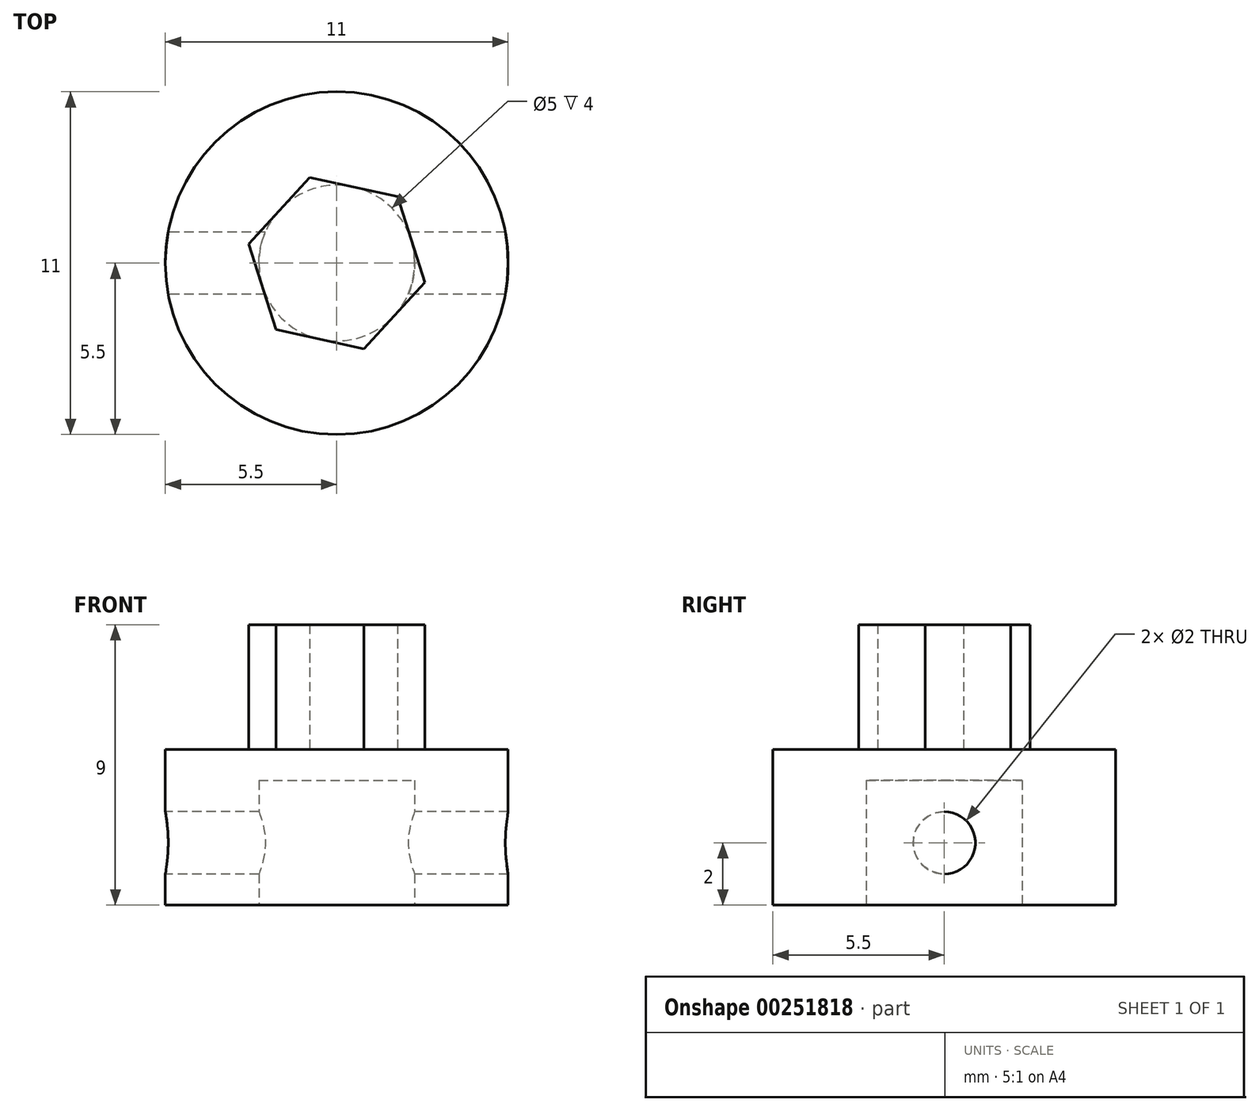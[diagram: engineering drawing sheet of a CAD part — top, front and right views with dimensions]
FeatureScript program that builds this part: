
annotation { "Feature Type Name" : "Feature", "Feature Type Description" : "" }
export const myFeature = defineFeature(function(context is Context, id is Id, definition is map)
    precondition{}
    {
        {
            var Q0;
            Q0=qCreatedBy(makeId("Top.planeOp"),FACE);
            var sketch = newSketch(context, id + "F0", { "sketchPlane" : qUnion([Q0])});
            skCircle(sketch, "E0", {"center": v(0, 0) * mm, "radius": 5.5 * mm});
            skSolve(sketch);
        }
        {
            var Q0;
            Q0=makeQuery(id+"F0.imprint","IMPRINT",FACE,{"disambiguationData":[TD([[makeQuery(id+"F0.imprint","IMPRINT",EDGE,{"derivedFrom":sQuery(id+"F0.wireOp",EDGE,"E0")}),1.0]])]});
            extrude(context, id + "F1", {"entities" : qUnion([Q0]), "endBound" : BoundingType.SYMMETRIC, "depth" : 5 * mm});
        }
        {
            var Q0;
            Q0=makeQuery(id+"F1.opExtrude","CAP_FACE",FACE,{"disambiguationData":[OSD([sQuery(id+"F0.wireOp",EDGE,"E0")])],"isStart":false});
            var sketch = newSketch(context, id + "F2", { "sketchPlane" : qUnion([Q0])});
            skCircle(sketch, "E1.cCircle", {"center": v(0, 0) * mm, "radius": 2.5 * mm, "construction": true});
            skLineSegment(sketch, "E1.0", {"start": v(2.82, -0.62) * mm, "end": v(0.88, -2.75) * mm});
            skLineSegment(sketch, "E1.1", {"start": v(0.88, -2.75) * mm, "end": v(-1.94, -2.13) * mm});
            skLineSegment(sketch, "E1.2", {"start": v(-1.94, -2.13) * mm, "end": v(-2.82, 0.62) * mm});
            skLineSegment(sketch, "E1.3", {"start": v(-2.82, 0.62) * mm, "end": v(-0.88, 2.75) * mm});
            skLineSegment(sketch, "E1.4", {"start": v(-0.88, 2.75) * mm, "end": v(1.94, 2.13) * mm});
            skLineSegment(sketch, "E1.5", {"start": v(1.94, 2.13) * mm, "end": v(2.82, -0.62) * mm});
            skPoint(sketch, "E1.0.midPoint", {"position": v(1.85, -1.68) * mm});
            skSolve(sketch);
        }
        {
            var Q0;
            Q0 = qSketchRegion(id + "F2", true);
            extrude(context, id + "F3", {"entities" : qUnion([Q0]), "operationType" : NewBodyOperationType.ADD, "depth" : 4 * mm});
        }
        {
            var Q0;
            Q0=qCreatedBy(makeId("Right.planeOp"),FACE);
            var sketch = newSketch(context, id + "F4", { "sketchPlane" : qUnion([Q0])});
            skLineSegment(sketch, "E2.0", {"start": v(-5.5, -2.5) * mm, "end": v(5.5, -2.5) * mm});
            skLineSegment(sketch, "E3.0", {"start": v(-5.5, 2.5) * mm, "end": v(5.5, 2.5) * mm});
            skPoint(sketch, "E4", {"position": v(0, -0.5) * mm});
            skCircle(sketch, "E5", {"center": v(0, -0.5) * mm, "radius": 1 * mm});
            skSolve(sketch);
        }
        {
            var Q0;
            Q0=makeQuery(id+"F1.opExtrude","CAP_FACE",FACE,{"disambiguationData":[OSD([sQuery(id+"F0.wireOp",EDGE,"E0")])],"isStart":true});
            var sketch = newSketch(context, id + "F5", { "sketchPlane" : qUnion([Q0])});
            skCircle(sketch, "E6", {"center": v(0, 0) * mm, "radius": 2.5 * mm});
            skSolve(sketch);
        }
        {
            var Q0;
            Q0=makeQuery(id+"F5.imprint","IMPRINT",FACE,{"disambiguationData":[TD([[makeQuery(id+"F5.imprint","IMPRINT",EDGE,{"derivedFrom":sQuery(id+"F5.wireOp",EDGE,"E6")}),1.0]])]});
            extrude(context, id + "F6", {"entities" : qUnion([Q0]), "operationType" : NewBodyOperationType.REMOVE, "oppositeDirection" : true, "depth" : 4 * mm});
        }
        {
            var Q0;
            Q0 = qSketchRegion(id + "F4", true);
            extrude(context, id + "F7", {"entities" : qUnion([Q0]), "operationType" : NewBodyOperationType.REMOVE, "endBound" : BoundingType.SYMMETRIC, "depth" : 25 * mm});
        }
    });
